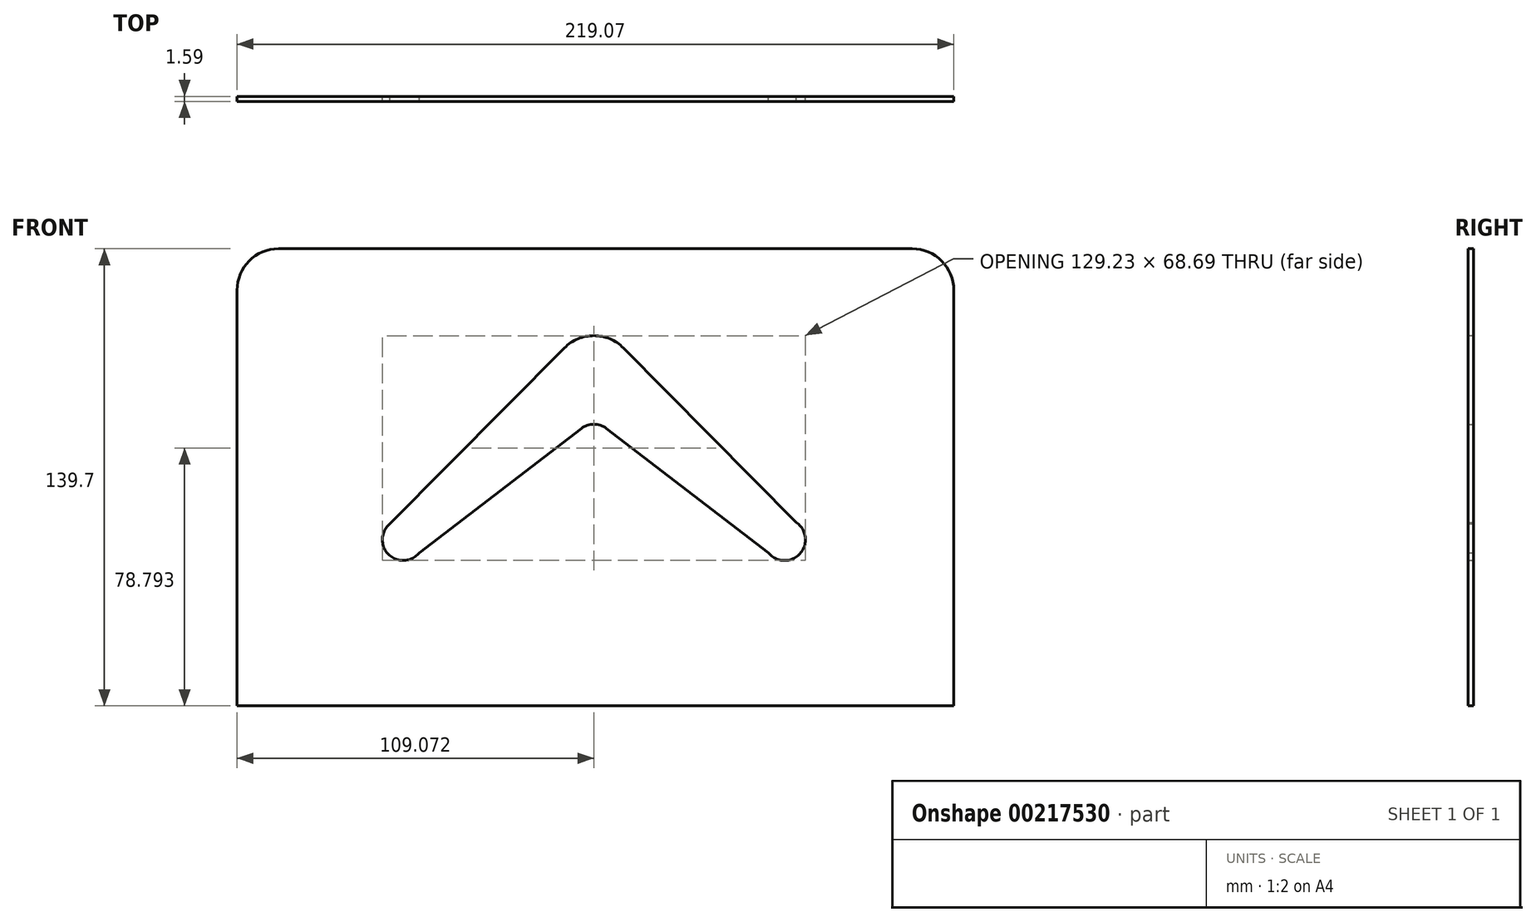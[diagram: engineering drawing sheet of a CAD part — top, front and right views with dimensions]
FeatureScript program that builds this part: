
annotation { "Feature Type Name" : "Feature", "Feature Type Description" : "" }
export const myFeature = defineFeature(function(context is Context, id is Id, definition is map)
    precondition{}
    {
        {
            var Q0;
            Q0=qCreatedBy(makeId("Front.planeOp"),FACE);
            var sketch = newSketch(context, id + "F0", { "sketchPlane" : qUnion([Q0])});
            skLineSegment(sketch, "E0.bottom", {"start": v(-96.4, 47.2) * mm, "end": v(97.28, 47.2) * mm});
            skLineSegment(sketch, "E0.top", {"start": v(-109.1, -92.5) * mm, "end": v(109.98, -92.5) * mm});
            skLineSegment(sketch, "E0.left", {"start": v(-109.1, 34.5) * mm, "end": v(-109.1, -92.5) * mm});
            skLineSegment(sketch, "E0.right", {"start": v(109.98, 34.5) * mm, "end": v(109.98, -92.5) * mm});
            skPoint(sketch, "E1.visualSharp", {"position": v(-109.1, 47.2) * mm});
            skArc(sketch, "E1.filletArc", {"start": v(-96.4, 47.2) * mm, "mid": v(-105.37, 43.48) * mm, "end": v(-109.1, 34.5) * mm});
            skPoint(sketch, "E2.visualSharp", {"position": v(109.98, 47.2) * mm});
            skArc(sketch, "E2.filletArc", {"start": v(109.98, 34.5) * mm, "mid": v(106.26, 43.48) * mm, "end": v(97.28, 47.2) * mm});
            skCircle(sketch, "E3", {"center": v(-58.3, -41.7) * mm, "radius": 6.35 * mm});
            skCircle(sketch, "E4", {"center": v(0, 7.94) * mm, "radius": 12.7 * mm});
            skCircle(sketch, "E5.MirrorC", {"center": v(58.3, -41.7) * mm, "radius": 6.35 * mm});
            skLineSegment(sketch, "E6", {"start": v(-62.33, -36.8) * mm, "end": v(-9.01, 16.89) * mm});
            skLineSegment(sketch, "E7", {"start": v(-62.33, -36.8) * mm, "end": v(-53.36, -45.7) * mm});
            skLineSegment(sketch, "E8", {"start": v(-53.36, -45.7) * mm, "end": v(-3.87, -7.73) * mm});
            skLineSegment(sketch, "E9", {"start": v(3.87, -7.73) * mm, "end": v(53.36, -45.7) * mm});
            skLineSegment(sketch, "E10", {"start": v(53.36, -45.7) * mm, "end": v(62.2, -36.8) * mm});
            skLineSegment(sketch, "E11", {"start": v(62.2, -36.8) * mm, "end": v(9.01, 16.89) * mm});
            skPoint(sketch, "E12.visualSharp", {"position": v(0, -4.76) * mm});
            skArc(sketch, "E12.filletArc", {"start": v(3.87, -7.73) * mm, "mid": v(0, -6.42) * mm, "end": v(-3.87, -7.73) * mm});
            skSolve(sketch);
        }
        {
            var Q0;
            Q0=makeQuery(id+"F0.imprint","IMPRINT",FACE,{"disambiguationData":[TD([[makeQuery(id+"F0.imprint","IMPRINT",EDGE,{"derivedFrom":sQuery(id+"F0.wireOp",EDGE,"E0.bottom")}),-1.0]])]});
            extrude(context, id + "F1", {"entities" : qUnion([Q0]), "depth" : 1.59 * mm});
        }
    });
